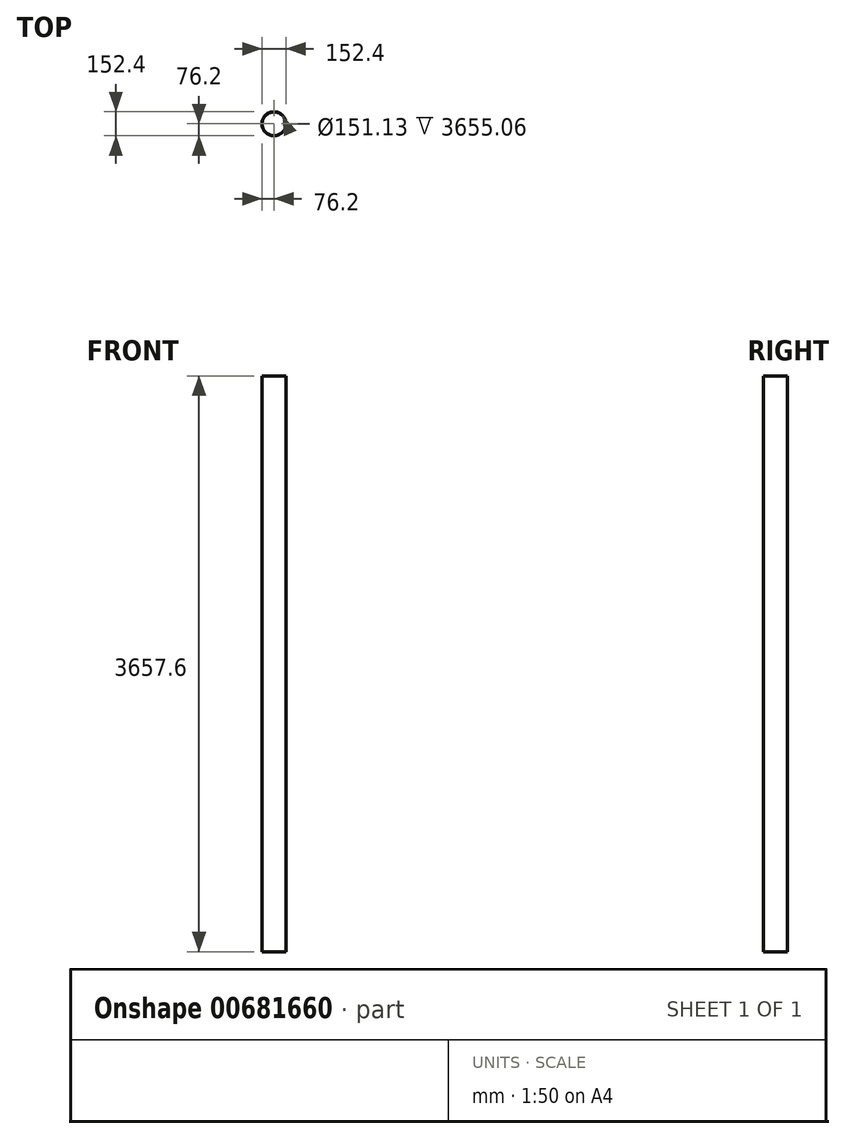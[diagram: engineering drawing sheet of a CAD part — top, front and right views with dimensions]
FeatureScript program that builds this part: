
annotation { "Feature Type Name" : "Feature", "Feature Type Description" : "" }
export const myFeature = defineFeature(function(context is Context, id is Id, definition is map)
    precondition{}
    {
        {
            var Q0;
            Q0=qCreatedBy(makeId("Top.planeOp"),FACE);
            var sketch = newSketch(context, id + "F0", { "sketchPlane" : qUnion([Q0])});
            skCircle(sketch, "E0", {"center": v(0, 0) * mm, "radius": 75.57 * mm});
            skCircle(sketch, "E1", {"center": v(0, 0) * mm, "radius": 76.2 * mm});
            skSolve(sketch);
        }
        {
            var Q0;
            Q0=makeQuery(id+"F0.imprint","IMPRINT",FACE,{"disambiguationData":[TD([[makeQuery(id+"F0.imprint","IMPRINT",EDGE,{"derivedFrom":sQuery(id+"F0.wireOp",EDGE,"E0")}),-1.0]])]});
            var Q1;
            Q1=makeQuery(id+"F0.imprint","IMPRINT",FACE,{"disambiguationData":[TD([[makeQuery(id+"F0.imprint","IMPRINT",EDGE,{"derivedFrom":sQuery(id+"F0.wireOp",EDGE,"E0")}),1.0]])]});
            extrude(context, id + "F1", {"entities" : qUnion([Q0, Q1]), "oppositeDirection" : true, "depth" : 3657.6 * mm, "offsetDistance" : 25.4 * mm});
        }
        {
            var Q0;
            Q0=makeQuery(id+"F0.imprint","IMPRINT",FACE,{"disambiguationData":[TD([[makeQuery(id+"F0.imprint","IMPRINT",EDGE,{"derivedFrom":sQuery(id+"F0.wireOp",EDGE,"E0")}),1.0]])]});
            var Q1;
            Q1=sQuery(id+"F0.wireOp",EDGE,"E0");
            extrude(context, id + "F2", {"entities" : qUnion([Q0]), "operationType" : NewBodyOperationType.REMOVE, "surfaceEntities" : qUnion([Q1]), "oppositeDirection" : true, "depth" : 3655.06 * mm, "offsetDistance" : 25.4 * mm});
        }
    });
